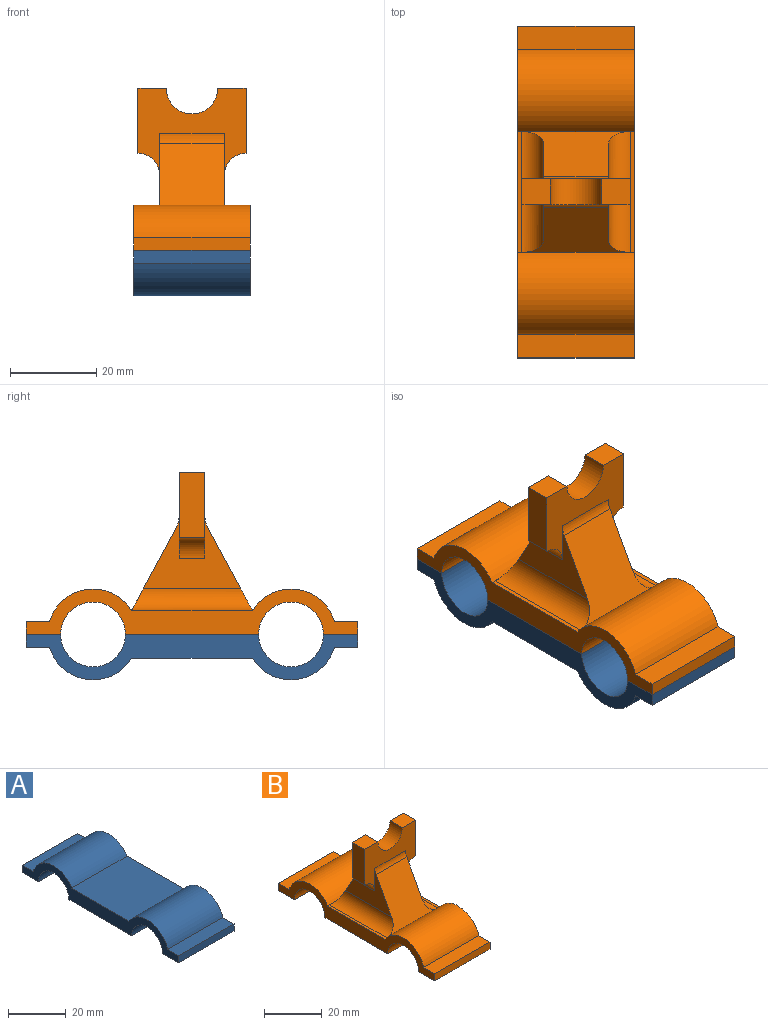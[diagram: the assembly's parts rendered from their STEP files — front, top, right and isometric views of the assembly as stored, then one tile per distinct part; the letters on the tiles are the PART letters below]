
ASSEMBLY  parts=2 mates=1
PART A: 14 faces, bbox 27x76.8x10.5 mm
  f0: plane 27x8mm, normal (0,0,-1), area 216mm2, adj f1,f11,f12,f13
  f1: cylinder r=7.5mm len=27mm, axis (-1,0,0), area 636.2mm2, adj f0,f2,f12,f13
  f2: plane 30.8x27mm, normal (0,0,-1), area 831.6mm2, adj f1,f3,f12,f13
  f3: cylinder r=7.5mm len=27mm, axis (-1,0,0), area 636.2mm2, adj f2,f4,f12,f13
  f4: plane 27x8mm, normal (0,0,-1), area 216mm2, adj f3,f5,f12,f13
  f5: plane 27x3mm, normal (0,1,0), area 81mm2, adj f4,f6,f12,f13
  f6: plane 27x5.44mm, normal (0,0,1), area 146.8mm2, adj f5,f7,f12,f13
  f7: cylinder r=10.5mm len=27mm, axis (-1,0,0), area 651mm2, adj f6,f8,f12,f13
  f8: plane 27.96x27mm, normal (0,0,1), area 754.9mm2, adj f7,f9,f12,f13
  f9: cylinder r=10.5mm len=27mm, axis (-1,0,0), area 651mm2, adj f8,f10,f12,f13
  f10: plane 27x5.44mm, normal (0,0,1), area 146.8mm2, adj f9,f11,f12,f13
  f11: plane 27x3mm, normal (0,-1,0), area 81mm2, adj f0,f10,f12,f13
  f12: plane 76.8x10.5mm, normal (1,0,0), area 343.5mm2, adj f0,f1,f2,f3,f4,f5,f6,f7
  f13: plane 76.8x10.5mm, normal (-1,0,0), area 343.5mm2, adj f0,f1,f2,f3,f4,f5,f6,f7
PART B: 32 faces, bbox 27x76.8x37.5 mm
  f0: plane 6.55x6mm, normal (0,0,1), area 39.3mm2, adj f20,f21,f24,f31
  f1: plane 27.96x1mm, normal (0,0,1), area 28mm2, adj f9,f11,f15,f27
  f2: plane 27x8mm, normal (0,0,-1), area 216mm2, adj f3,f13,f14,f15
  f3: cylinder r=7.5mm len=27mm, axis (-1,0,0), area 636.2mm2, adj f2,f4,f14,f15
  f4: plane 30.8x27mm, normal (0,0,-1), area 831.6mm2, adj f3,f5,f14,f15
  f5: cylinder r=7.5mm len=27mm, axis (-1,0,0), area 636.2mm2, adj f4,f6,f14,f15
  f6: plane 27x8mm, normal (0,0,-1), area 216mm2, adj f5,f7,f14,f15
  f7: plane 27x3mm, normal (0,1,0), area 81mm2, adj f6,f8,f14,f15
  f8: plane 27x5.44mm, normal (0,0,1), area 146.8mm2, adj f7,f9,f14,f15
  f9: cylinder r=10.5mm len=27mm, axis (-1,0,0), area 651mm2, adj f1,f8,f10,f14,f15,f17
  f10: plane 27.96x1mm, normal (0,0,1), area 28mm2, adj f9,f11,f14,f29
  f11: cylinder r=10.5mm len=27mm, axis (-1,0,0), area 651mm2, adj f1,f10,f12,f14,f15,f16
  f12: plane 27x5.44mm, normal (0,0,1), area 146.8mm2, adj f11,f13,f14,f15
  f13: plane 27x3mm, normal (0,-1,0), area 81mm2, adj f2,f12,f14,f15
  f14: plane 76.8x10.5mm, normal (1,0,0), area 343.5mm2, adj f2,f3,f4,f5,f6,f7,f8,f9
  f15: plane 76.8x10.5mm, normal (-1,0,0), area 343.5mm2, adj f1,f2,f3,f4,f5,f6,f7,f8
  f16: plane 25x19.18mm, normal (0,-0.88,0.48), area 339.4mm2, adj f11,f18,f19,f25,f27,f29
  f17: plane 25x19.18mm, normal (0,0.88,0.48), area 339.4mm2, adj f9,f18,f19,f26,f27,f29
  f18: plane 22.55x16.56mm, normal (1,0,0), area 168.4mm2, adj f16,f17,f20,f21,f25,f26,f29,f30
  f19: plane 22.55x16.56mm, normal (-1,0,0), area 168.4mm2, adj f16,f17,f20,f21,f25,f26,f27,f28
  f20: plane 25x20.05mm, normal (0,-1,0), area 262mm2, adj f0,f18,f19,f22,f23,f24,f25,f28
  f21: plane 25x20.05mm, normal (0,1,0), area 262mm2, adj f0,f18,f19,f22,f23,f24,f26,f28
  f22: plane 6.55x6mm, normal (0,0,1), area 39.3mm2, adj f20,f21,f23,f31
  f23: plane 15.05x6mm, normal (1,0,0), area 90.3mm2, adj f20,f21,f22,f30
  f24: plane 15.05x6mm, normal (-1,0,0), area 90.3mm2, adj f0,f20,f21,f28
  f25: cylinder r=5mm len=15mm, axis (1,0,0), area 37.2mm2, adj f16,f18,f19,f20
  f26: cylinder r=5mm len=15mm, axis (-1,0,0), area 37.2mm2, adj f17,f18,f19,f21
  f27: cylinder r=5mm len=27.96mm, axis (0,1,0), area 204.2mm2, adj f1,f16,f17,f19
  f28: cylinder r=5mm len=6mm, axis (0,-1,0), area 47.1mm2, adj f19,f20,f21,f24
  f29: cylinder r=5mm len=27.96mm, axis (0,-1,0), area 204.2mm2, adj f10,f16,f17,f18
  f30: cylinder r=5mm len=6mm, axis (0,1,0), area 47.1mm2, adj f18,f20,f21,f23
  f31: cylinder r=5.95mm len=11.9mm, axis (0,1,0), area 112.2mm2, adj f0,f20,f21,f22
PLACE A rot(axis=(0,1,0),180deg) t=(-25.28,0.92,4.51)mm
PLACE B t=(-25.28,0.92,4.51)mm
MATE parallel A.f2 <-> B.f4  axis (0,0,1) through (-25.28,0.92,4.51)mm
